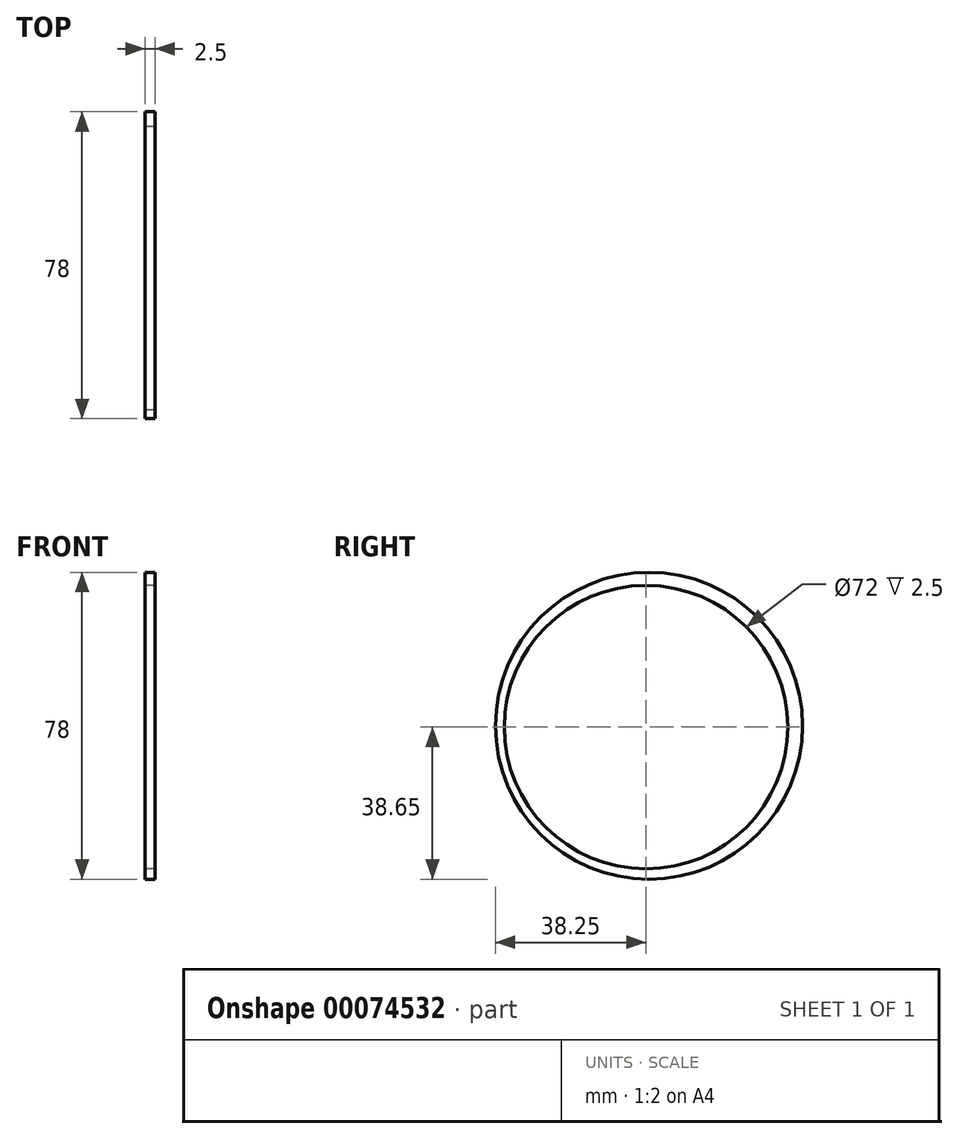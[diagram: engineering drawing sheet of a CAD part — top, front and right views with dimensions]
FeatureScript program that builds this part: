
annotation { "Feature Type Name" : "Feature", "Feature Type Description" : "" }
export const myFeature = defineFeature(function(context is Context, id is Id, definition is map)
    precondition{}
    {
        {
            var Q0;
            Q0=qCreatedBy(makeId("Right.planeOp"),FACE);
            var sketch = newSketch(context, id + "F0", { "sketchPlane" : qUnion([Q0])});
            skCircle(sketch, "E0", {"center": v(0, 0) * mm, "radius": 36 * mm});
            skCircle(sketch, "E1", {"center": v(0.75, 0.35) * mm, "radius": 39 * mm});
            skSolve(sketch);
        }
        {
            var Q0;
            Q0=makeQuery(id+"F0.imprint","IMPRINT",FACE,{"disambiguationData":[TD([[makeQuery(id+"F0.imprint","IMPRINT",EDGE,{"derivedFrom":sQuery(id+"F0.wireOp",EDGE,"E0")}),-1.0]])]});
            extrude(context, id + "F1", {"entities" : qUnion([Q0]), "depth" : 2.5 * mm});
        }
    });
